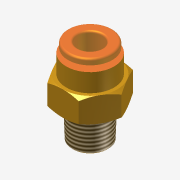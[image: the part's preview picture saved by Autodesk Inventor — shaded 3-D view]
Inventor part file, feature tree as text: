
AUTODESK INVENTOR PART (.ipt)
format: ipt  version: 2014 SP1 (Build 180222100, 222)  size: 166,912 bytes
history: native  units: mm
features: imported_body x1, thread x1
ambient origin geometry x8: Origin, YZ Plane, XZ Plane, XY Plane, X Axis, Y Axis, Z Axis, Center Point
bodies: Solid1 (feature_tree)
feature tree (2):
  imported_body  "Base1"
  thread  "Thread1"  [1 undecoded]
note: 1 required parameter value undecoded (feature->parameter linkage not recoverable at this tier; creation-order binding heuristic only, values carry confidence <= 0.55)
